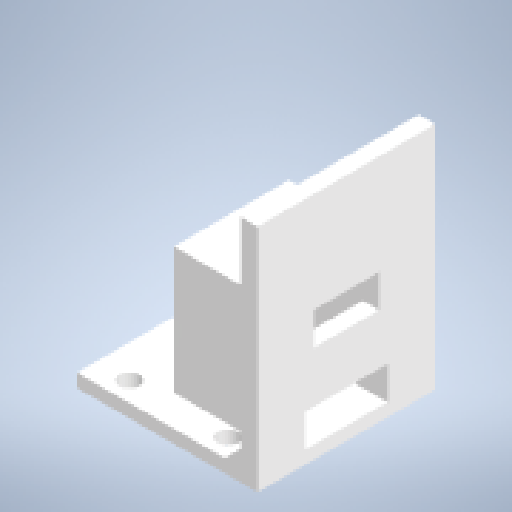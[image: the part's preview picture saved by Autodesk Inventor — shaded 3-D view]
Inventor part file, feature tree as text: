
AUTODESK INVENTOR PART (.ipt)
format: ipt  version: 2025 (Build 290162000, 162)  size: 348,160 bytes
history: native  units: mm
features: extrude x9, sketch x4, other x1, projected_geometry x1
ambient origin geometry x8: Origin, YZ Plane, XZ Plane, XY Plane, X Axis, Y Axis, Z Axis, Center Point
bodies: Body1 (feature_tree)
feature tree (15):
  other  "Bryła1"
  sketch  "Szkic1"
  extrude  "Wyciągnięcie proste1"  Depth=50.0mm
  extrude  "Wyciągnięcie proste2"  Depth=10.0mm
  extrude  "Wyciągnięcie proste3"  Depth=6.0mm
  extrude  "Wyciągnięcie proste4"  Depth=6.0mm
  extrude  "Wyciągnięcie proste5"  Depth=5.0mm
  extrude  "Wyciągnięcie proste6"  Depth=54.0mm
  extrude  "Wyciągnięcie proste7"  Depth=54.0mm
  extrude  "Wyciągnięcie proste8"  Depth=4.0mm TaperAngle=0.0deg
  extrude  "Wyciągnięcie proste9"  Depth=70.0mm TaperAngle=0.0deg
  sketch  "Szkic3"
  sketch  "Szkic9"
  sketch  "Szkic10"
  projected_geometry  "Pętla rzutowana1"
